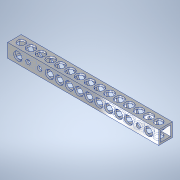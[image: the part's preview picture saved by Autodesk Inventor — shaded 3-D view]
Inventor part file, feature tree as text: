
AUTODESK INVENTOR PART (.ipt)
format: ipt  version: 2020.3 (Build 243373000, 373)  size: 231,424 bytes
history: native  units: mm
features: sketch x6, hole x5, other x1, extrude x1
ambient origin geometry x8: Origin, YZ Plane, XZ Plane, XY Plane, X Axis, Y Axis, Z Axis, Center Point
bodies: Body1 (feature_tree)
feature tree (13):
  other  "ソリッド1"
  extrude  "押し出し1"  Depth=9.0mm
  hole  "穴1"  [1 undecoded]
  hole  "穴2"  [1 undecoded]
  hole  "穴4"  [1 undecoded]
  hole  "穴5"  [1 undecoded]
  hole  "穴6"  [1 undecoded]
  sketch  "スケッチ1"
  sketch  "スケッチ2"
  sketch  "スケッチ3"
  sketch  "スケッチ5"
  sketch  "スケッチ6"
  sketch  "スケッチ7"
note: 5 required parameter values undecoded (feature->parameter linkage not recoverable at this tier; creation-order binding heuristic only, values carry confidence <= 0.55)
